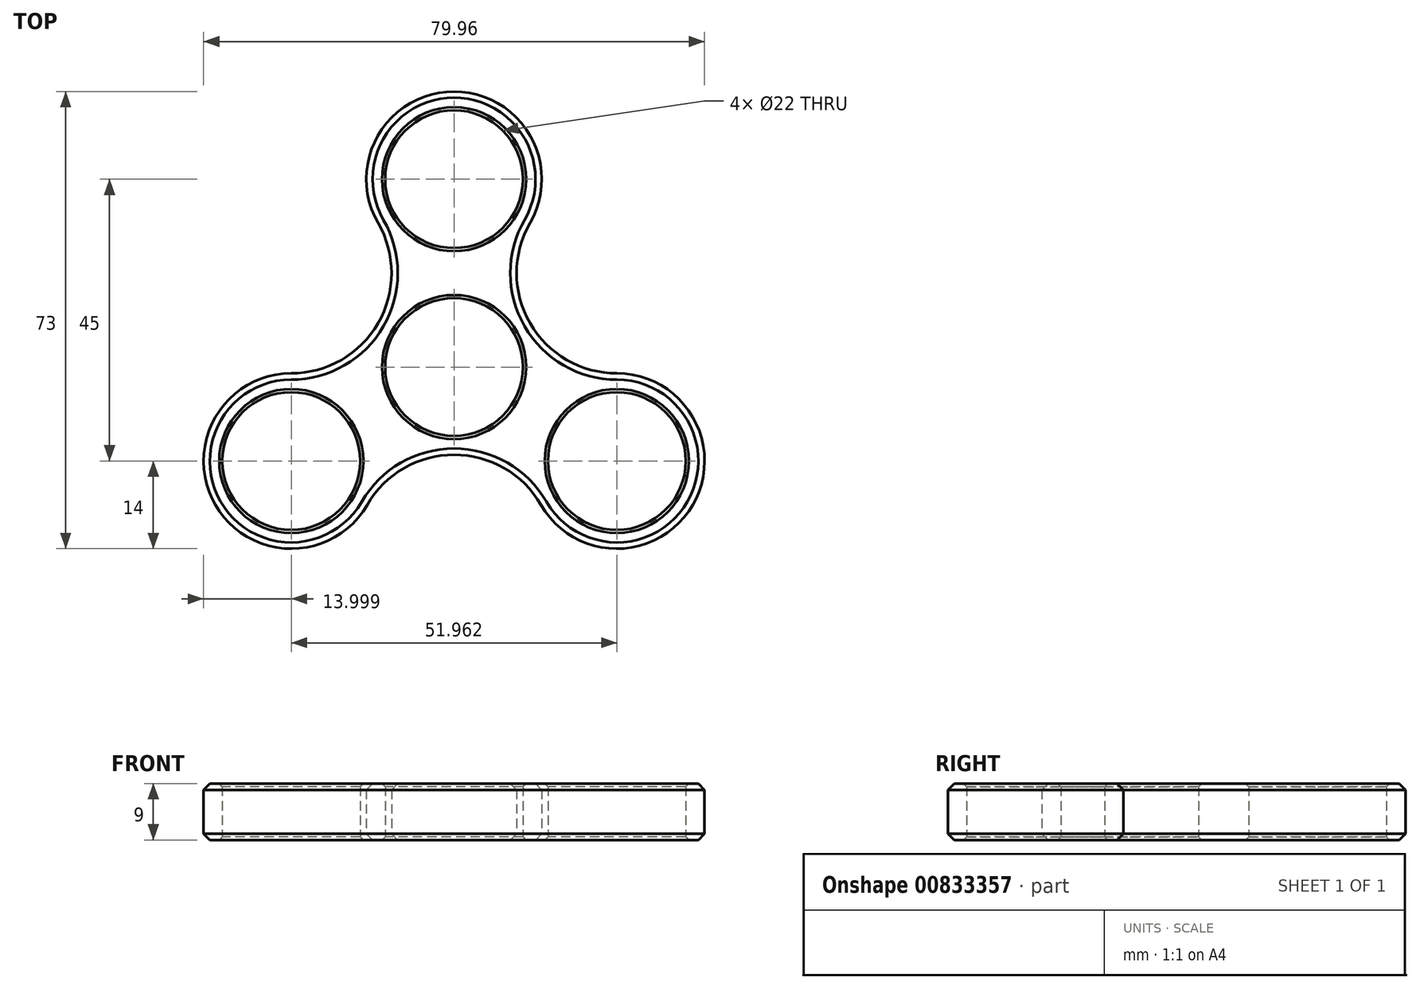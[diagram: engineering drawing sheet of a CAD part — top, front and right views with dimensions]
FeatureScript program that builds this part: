
annotation { "Feature Type Name" : "Feature", "Feature Type Description" : "" }
export const myFeature = defineFeature(function(context is Context, id is Id, definition is map)
    precondition{}
    {
        {
            assignVariable(context, id + "F0", {"name" : "extrude", "anyValue" : 9});
        }
        {
            var Q0;
            Q0=qCreatedBy(makeId("Top.planeOp"),FACE);
            var sketch = newSketch(context, id + "F1", { "sketchPlane" : qUnion([Q0])});
            skCircle(sketch, "E0", {"center": v(0, 30) * mm, "radius": 11 * mm});
            skCircle(sketch, "E1", {"center": v(0, 0) * mm, "radius": 11 * mm});
            skCircle(sketch, "E2.1.0", {"center": v(-25.98, -15) * mm, "radius": 11 * mm});
            skCircle(sketch, "E2.2.0", {"center": v(25.98, -15) * mm, "radius": 11 * mm});
            skCircle(sketch, "E3", {"center": v(0, 30) * mm, "radius": 14 * mm});
            skCircle(sketch, "E4.1.0", {"center": v(-25.98, -15) * mm, "radius": 14 * mm});
            skCircle(sketch, "E4.2.0", {"center": v(25.98, -15) * mm, "radius": 14 * mm});
            skCircle(sketch, "E5", {"center": v(0, 0) * mm, "radius": 14 * mm});
            skCircle(sketch, "E6", {"center": v(25.98, 15) * mm, "radius": 16 * mm});
            skPoint(sketch, "E6.first.point", {"position": v(12.12, 23) * mm});
            skPoint(sketch, "E6.second.point", {"position": v(12.12, 7) * mm});
            skPoint(sketch, "E6.third.point", {"position": v(25.98, -1) * mm});
            skCircle(sketch, "E7.1.0", {"center": v(-25.98, 15) * mm, "radius": 16 * mm});
            skCircle(sketch, "E7.2.0", {"center": v(0, -30) * mm, "radius": 16 * mm});
            skSolve(sketch);
        }
        {
            var Q0;
            Q0=makeQuery(id+"F1.imprint","IMPRINT",FACE,{"disambiguationData":[TD([[makeQuery(id+"F1.imprint","IMPRINT",EDGE,{"derivedFrom":sQuery(id+"F1.wireOp",EDGE,"E0")}),-1.0]])]});
            var Q1;
            Q1=makeQuery(id+"F1.imprint","IMPRINT",FACE,{"disambiguationData":[TD([[makeQuery(id+"F1.imprint","IMPRINT",EDGE,{"derivedFrom":sQuery(id+"F1.wireOp",EDGE,"E2.2.0")}),-1.0]])]});
            var Q2;
            Q2=makeQuery(id+"F1.imprint","IMPRINT",FACE,{"disambiguationData":[TD([[makeQuery(id+"F1.imprint","IMPRINT",EDGE,{"derivedFrom":sQuery(id+"F1.wireOp",EDGE,"E2.1.0")}),-1.0]])]});
            var Q3;
            {var subQ0=sQuery(id+"F1.wireOp",EDGE,"E7.1.0");var subQ1=sQuery(id+"F1.wireOp",EDGE,"E4.1.0");var subQ2=makeQuery(id+"F1.imprint","INTERSECT",VERTEX,{"derivedFrom":[subQ1,subQ0]});Q3=makeQuery(id+"F1.imprint","IMPRINT",FACE,{"disambiguationData":[TD([[makeQuery(id+"F1.imprint","IMPRINT",EDGE,{"disambiguationData":[TD([[subQ2,1.0]])],"derivedFrom":subQ1}),-1.0]])]});}
            var Q4;
            {var subQ0=sQuery(id+"F1.wireOp",EDGE,"E6");var subQ1=sQuery(id+"F1.wireOp",EDGE,"E4.2.0");var subQ2=makeQuery(id+"F1.imprint","INTERSECT",VERTEX,{"derivedFrom":[subQ1,subQ0]});Q4=makeQuery(id+"F1.imprint","IMPRINT",FACE,{"disambiguationData":[TD([[makeQuery(id+"F1.imprint","IMPRINT",EDGE,{"disambiguationData":[TD([[subQ2,-1.0]])],"derivedFrom":subQ1}),-1.0]])]});}
            var Q5;
            {var subQ0=sQuery(id+"F1.wireOp",EDGE,"E6");var subQ1=sQuery(id+"F1.wireOp",EDGE,"E3");var subQ2=makeQuery(id+"F1.imprint","INTERSECT",VERTEX,{"derivedFrom":[subQ1,subQ0]});Q5=makeQuery(id+"F1.imprint","IMPRINT",FACE,{"disambiguationData":[TD([[makeQuery(id+"F1.imprint","IMPRINT",EDGE,{"disambiguationData":[TD([[subQ2,1.0]])],"derivedFrom":subQ1}),-1.0]])]});}
            var Q6;
            Q6=makeQuery(id+"F1.imprint","IMPRINT",FACE,{"disambiguationData":[TD([[makeQuery(id+"F1.imprint","IMPRINT",EDGE,{"derivedFrom":sQuery(id+"F1.wireOp",EDGE,"E1")}),-1.0]])]});
            extrude(context, id + "F2", {"entities" : qUnion([Q0, Q1, Q2, Q3, Q4, Q5, Q6]), "depth" : (getVariable(context, 'extrude')) * mm, "offsetDistance" : 25 * mm});
        }
        {
            var Q0;
            Q0=makeQuery(id+"F2.opExtrude","CAP_EDGE",EDGE,{"disambiguationData":[OSD([sQuery(id+"F1.wireOp",EDGE,"E2.1.0")])],"isStart":false});
            var Q1;
            Q1=makeQuery(id+"F2.opExtrude","CAP_EDGE",EDGE,{"disambiguationData":[OSD([sQuery(id+"F1.wireOp",EDGE,"E1")])],"isStart":false});
            var Q2;
            Q2=makeQuery(id+"F2.opExtrude","CAP_EDGE",EDGE,{"disambiguationData":[OSD([sQuery(id+"F1.wireOp",EDGE,"E0")])],"isStart":false});
            var Q3;
            Q3=makeQuery(id+"F2.opExtrude","CAP_EDGE",EDGE,{"disambiguationData":[OSD([sQuery(id+"F1.wireOp",EDGE,"E2.2.0")])],"isStart":false});
            var Q4;
            Q4=makeQuery(id+"F2.opExtrude","CAP_EDGE",EDGE,{"disambiguationData":[OSD([sQuery(id+"F1.wireOp",EDGE,"E2.1.0")])],"isStart":true});
            var Q5;
            Q5=makeQuery(id+"F2.opExtrude","CAP_EDGE",EDGE,{"disambiguationData":[OSD([sQuery(id+"F1.wireOp",EDGE,"E1")])],"isStart":true});
            var Q6;
            Q6=makeQuery(id+"F2.opExtrude","CAP_EDGE",EDGE,{"disambiguationData":[OSD([sQuery(id+"F1.wireOp",EDGE,"E2.2.0")])],"isStart":true});
            var Q7;
            Q7=makeQuery(id+"F2.opExtrude","CAP_EDGE",EDGE,{"disambiguationData":[OSD([sQuery(id+"F1.wireOp",EDGE,"E0")])],"isStart":true});
            chamfer(context, id + "F3", {"entities" : qUnion([Q0, Q1, Q2, Q3, Q4, Q5, Q6, Q7]), "width" : 0.5 * mm, "tangentPropagation" : true});
        }
        {
            var Q0;
            Q0=makeQuery(id+"F2.opExtrude","CAP_EDGE",EDGE,{"disambiguationData":[OSD([sQuery(id+"F1.wireOp",EDGE,"E4.1.0")])],"isStart":false});
            var Q1;
            Q1=makeQuery(id+"F2.opExtrude","CAP_EDGE",EDGE,{"disambiguationData":[OSD([sQuery(id+"F1.wireOp",EDGE,"E7.2.0")])],"isStart":false});
            var Q2;
            Q2=makeQuery(id+"F2.opExtrude","CAP_EDGE",EDGE,{"disambiguationData":[OSD([sQuery(id+"F1.wireOp",EDGE,"E7.1.0")])],"isStart":false});
            var Q3;
            Q3=makeQuery(id+"F2.opExtrude","CAP_EDGE",EDGE,{"disambiguationData":[OSD([sQuery(id+"F1.wireOp",EDGE,"E3")])],"isStart":false});
            var Q4;
            Q4=makeQuery(id+"F2.opExtrude","CAP_EDGE",EDGE,{"disambiguationData":[OSD([sQuery(id+"F1.wireOp",EDGE,"E6")])],"isStart":false});
            var Q5;
            Q5=makeQuery(id+"F2.opExtrude","CAP_EDGE",EDGE,{"disambiguationData":[OSD([sQuery(id+"F1.wireOp",EDGE,"E4.2.0")])],"isStart":false});
            var Q6;
            Q6=makeQuery(id+"F2.opExtrude","CAP_EDGE",EDGE,{"disambiguationData":[OSD([sQuery(id+"F1.wireOp",EDGE,"E7.2.0")])],"isStart":true});
            var Q7;
            Q7=makeQuery(id+"F2.opExtrude","CAP_EDGE",EDGE,{"disambiguationData":[OSD([sQuery(id+"F1.wireOp",EDGE,"E4.1.0")])],"isStart":true});
            var Q8;
            Q8=makeQuery(id+"F2.opExtrude","CAP_EDGE",EDGE,{"disambiguationData":[OSD([sQuery(id+"F1.wireOp",EDGE,"E7.1.0")])],"isStart":true});
            var Q9;
            Q9=makeQuery(id+"F2.opExtrude","CAP_EDGE",EDGE,{"disambiguationData":[OSD([sQuery(id+"F1.wireOp",EDGE,"E3")])],"isStart":true});
            var Q10;
            Q10=makeQuery(id+"F2.opExtrude","CAP_EDGE",EDGE,{"disambiguationData":[OSD([sQuery(id+"F1.wireOp",EDGE,"E6")])],"isStart":true});
            var Q11;
            Q11=makeQuery(id+"F2.opExtrude","CAP_EDGE",EDGE,{"disambiguationData":[OSD([sQuery(id+"F1.wireOp",EDGE,"E4.2.0")])],"isStart":true});
            chamfer(context, id + "F4", {"entities" : qUnion([Q0, Q1, Q2, Q3, Q4, Q5, Q6, Q7, Q8, Q9, Q10, Q11]), "width" : 1 * mm, "tangentPropagation" : true});
        }
    });
